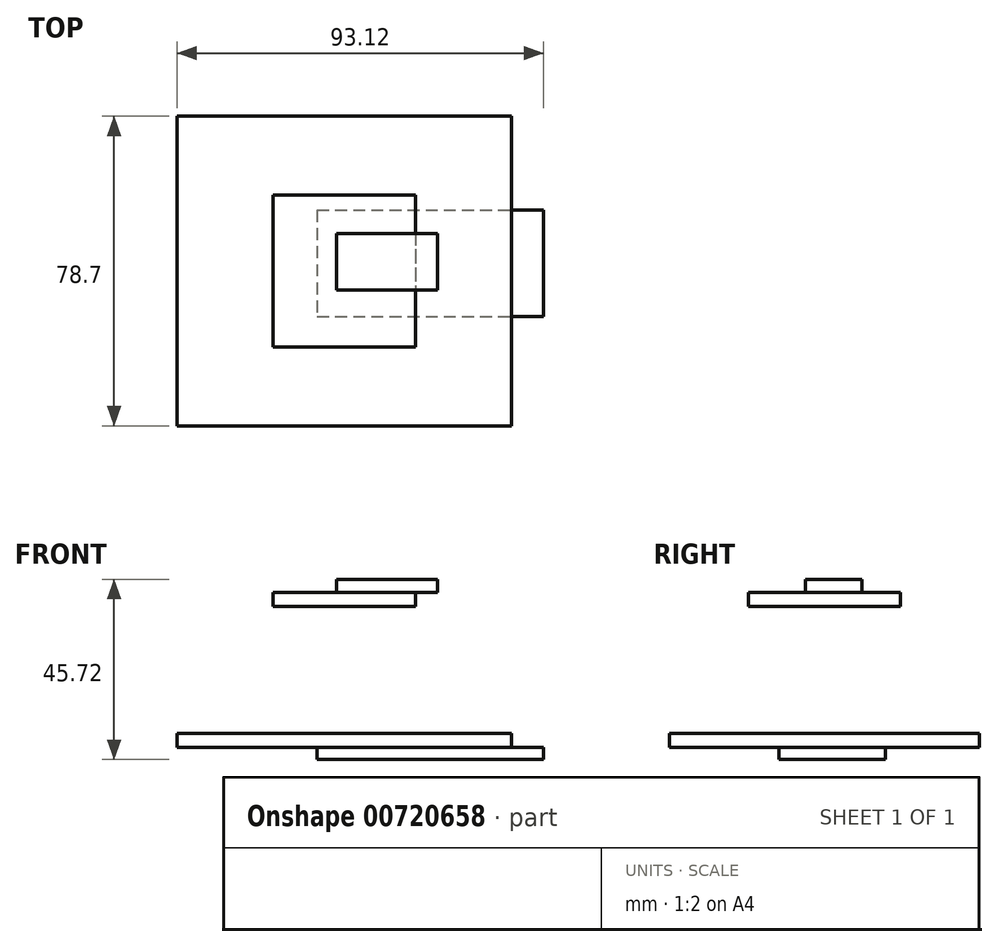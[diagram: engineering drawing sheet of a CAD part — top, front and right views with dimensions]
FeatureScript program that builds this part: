
annotation { "Feature Type Name" : "Feature", "Feature Type Description" : "" }
export const myFeature = defineFeature(function(context is Context, id is Id, definition is map)
    precondition{}
    {
        {
            var Q0;
            Q0=qCreatedBy(makeId("Top.planeOp"),FACE);
            var sketch = newSketch(context, id + "F0", { "sketchPlane" : qUnion([Q0])});
            skLineSegment(sketch, "E0.bottom", {"start": v(42.52, -39.35) * mm, "end": v(-42.52, -39.35) * mm});
            skLineSegment(sketch, "E0.top", {"start": v(42.52, 39.35) * mm, "end": v(-42.52, 39.35) * mm});
            skLineSegment(sketch, "E0.left", {"start": v(42.52, -39.35) * mm, "end": v(42.52, 39.35) * mm});
            skLineSegment(sketch, "E0.right", {"start": v(-42.52, -39.35) * mm, "end": v(-42.52, 39.35) * mm});
            skPoint(sketch, "E0.middle", {"position": v(0, 0) * mm});
            skSolve(sketch);
        }
        {
            var Q0;
            Q0=qCreatedBy(makeId("Top.planeOp"),FACE);
            cPlane(context, id + "F1", {"entities" : qUnion([Q0]), "cplaneType" : CPlaneType.OFFSET, "offset" : 32.26 * mm, "width" : 152.4 * mm, "height" : 152.4 * mm});
        }
        {
            var Q0;
            Q0=qCreatedBy(id+"F1.planeOp",FACE);
            var sketch = newSketch(context, id + "F2", { "sketchPlane" : qUnion([Q0])});
            skLineSegment(sketch, "E1.bottom", {"start": v(-18.06, 19.34) * mm, "end": v(18.06, 19.34) * mm});
            skLineSegment(sketch, "E1.top", {"start": v(-18.06, -19.34) * mm, "end": v(18.06, -19.34) * mm});
            skLineSegment(sketch, "E1.left", {"start": v(-18.06, 19.34) * mm, "end": v(-18.06, -19.34) * mm});
            skLineSegment(sketch, "E1.right", {"start": v(18.06, 19.34) * mm, "end": v(18.06, -19.34) * mm});
            skPoint(sketch, "E1.middle", {"position": v(0, 0) * mm});
            skSolve(sketch);
        }
        {
            var Q0;
            Q0 = qSketchRegion(id + "F2", true);
            extrude(context, id + "F3", {"entities" : qUnion([Q0]), "depth" : 3.56 * mm, "offsetDistance" : 25.4 * mm});
        }
        {
            var Q0;
            Q0=makeQuery(id+"F0.imprint","IMPRINT",FACE,{"disambiguationData":[TD([[makeQuery(id+"F0.imprint","IMPRINT",EDGE,{"derivedFrom":sQuery(id+"F0.wireOp",EDGE,"E0.bottom")}),-1.0]])]});
            extrude(context, id + "F4", {"entities" : qUnion([Q0]), "oppositeDirection" : true, "depth" : 3.56 * mm, "offsetDistance" : 25.4 * mm});
        }
        {
            var Q0;
            Q0=makeQuery(id+"F3.opExtrude","CAP_FACE",FACE,{"disambiguationData":[OSD([sQuery(id+"F2.wireOp",EDGE,"E1.bottom"),sQuery(id+"F2.wireOp",EDGE,"E1.top"),sQuery(id+"F2.wireOp",EDGE,"E1.left"),sQuery(id+"F2.wireOp",EDGE,"E1.right")])],"isStart":false});
            var sketch = newSketch(context, id + "F5", { "sketchPlane" : qUnion([Q0])});
            skLineSegment(sketch, "E2.bottom", {"start": v(-1.96, 9.53) * mm, "end": v(23.61, 9.53) * mm});
            skLineSegment(sketch, "E2.top", {"start": v(-1.96, -4.82) * mm, "end": v(23.61, -4.82) * mm});
            skLineSegment(sketch, "E2.left", {"start": v(-1.96, 9.53) * mm, "end": v(-1.96, -4.82) * mm});
            skLineSegment(sketch, "E2.right", {"start": v(23.61, 9.53) * mm, "end": v(23.61, -4.82) * mm});
            skSolve(sketch);
        }
        {
            var Q0;
            {var subQ0=sQuery(id+"F5.wireOp",EDGE,"E2.left");Q0=makeQuery(id+"F5.imprint","IMPRINT",FACE,{"disambiguationData":[TD([[makeQuery(id+"F5.imprint","IMPRINT",EDGE,{"derivedFrom":subQ0}),1.0]])]});}
            var Q1;
            {var subQ0=sQuery(id+"F5.wireOp",EDGE,"E2.right");Q1=makeQuery(id+"F5.imprint","IMPRINT",FACE,{"disambiguationData":[TD([[makeQuery(id+"F5.imprint","IMPRINT",EDGE,{"derivedFrom":subQ0}),-1.0]])]});}
            extrude(context, id + "F6", {"entities" : qUnion([Q0, Q1]), "operationType" : NewBodyOperationType.ADD, "depth" : 3.3 * mm, "offsetDistance" : 25.4 * mm});
        }
        {
            var Q0;
            Q0=makeQuery(id+"F4.opExtrude","CAP_FACE",FACE,{"disambiguationData":[OSD([sQuery(id+"F0.wireOp",EDGE,"E0.bottom"),sQuery(id+"F0.wireOp",EDGE,"E0.top"),sQuery(id+"F0.wireOp",EDGE,"E0.left"),sQuery(id+"F0.wireOp",EDGE,"E0.right")])],"isStart":false});
            var sketch = newSketch(context, id + "F7", { "sketchPlane" : qUnion([Q0])});
            skLineSegment(sketch, "E3.bottom", {"start": v(-6.91, -15.49) * mm, "end": v(50.6, -15.49) * mm});
            skLineSegment(sketch, "E3.top", {"start": v(-6.91, 11.6) * mm, "end": v(50.6, 11.6) * mm});
            skLineSegment(sketch, "E3.left", {"start": v(-6.91, -15.49) * mm, "end": v(-6.91, 11.6) * mm});
            skLineSegment(sketch, "E3.right", {"start": v(50.6, -15.49) * mm, "end": v(50.6, 11.6) * mm});
            skSolve(sketch);
        }
        {
            var Q0;
            {var subQ0=sQuery(id+"F7.wireOp",EDGE,"E3.right");Q0=makeQuery(id+"F7.imprint","IMPRINT",FACE,{"disambiguationData":[TD([[makeQuery(id+"F7.imprint","IMPRINT",EDGE,{"derivedFrom":subQ0}),1.0]])]});}
            var Q1;
            {var subQ0=sQuery(id+"F7.wireOp",EDGE,"E3.left");Q1=makeQuery(id+"F7.imprint","IMPRINT",FACE,{"disambiguationData":[TD([[makeQuery(id+"F7.imprint","IMPRINT",EDGE,{"derivedFrom":subQ0}),-1.0]])]});}
            extrude(context, id + "F8", {"entities" : qUnion([Q0, Q1]), "operationType" : NewBodyOperationType.ADD, "depth" : 3.05 * mm, "offsetDistance" : 25.4 * mm});
        }
    });
